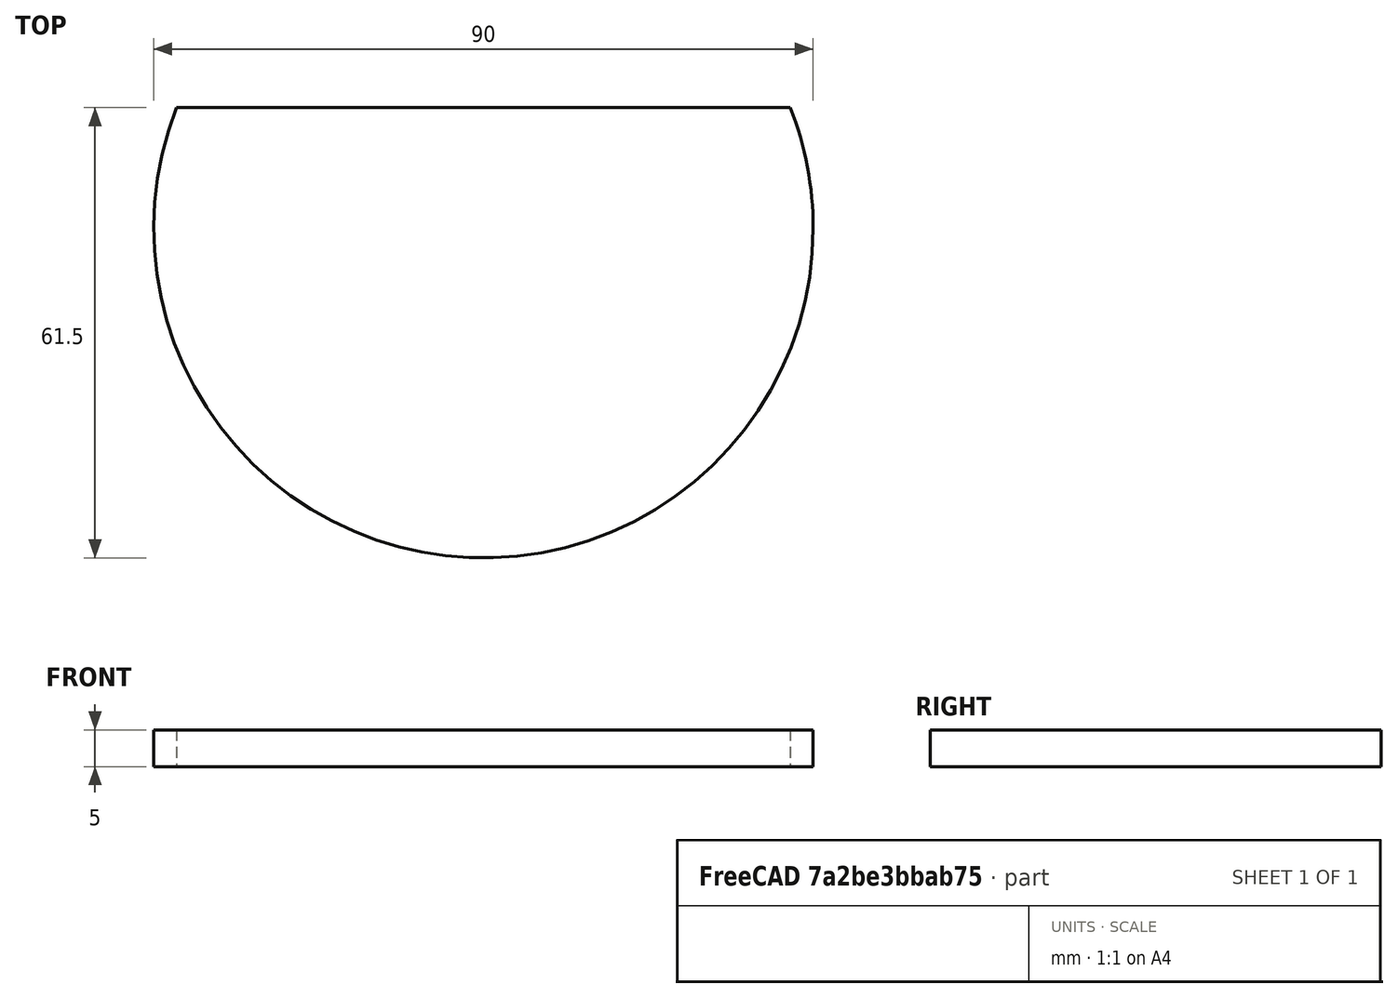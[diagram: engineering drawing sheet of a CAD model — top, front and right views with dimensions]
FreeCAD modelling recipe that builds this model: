
FCSTD DOCUMENT  (FreeCAD 1.0R39319 (Git))
Label: chapa_circle_90mm
License: All rights reserved
LicenseURL: https://en.wikipedia.org/wiki/All_rights_reserved
objects: Sketcher::SketchObject×2, PartDesign::Pad×1, PartDesign::Pocket×1, PartDesign::Body×1
note: 11 computed .brp shape members not serialized (recipe doc carries the construction recipe); baked Part::Feature solids carry a one-line shape summary decoded from their .brp

FEATURE [Sketcher::SketchObject] Sketch_1
  ArcFitTolerance = 1e-06
  AttachmentSupport = -> [XY_Plane]
  FullyConstrained = false
  MakeInternals = false
  MapMode = 5
  sketch-geometry (1):
    g0: Circle CenterX=0 CenterY=0 CenterZ=0 NormalX=0 NormalY=0 NormalZ=1 AngleXU=0 Radius=45
FEATURE [PartDesign::Pad] Pad_1
  Direction = (0,0,1)
  Length = 5
  Length2 = 10
  Profile = -> Sketch_1
  Refine = true
  Suppressed = false
  Type = 0
FEATURE [Sketcher::SketchObject] Sketch_2
  ArcFitTolerance = 1e-06
  AttachmentSupport = -> [Pad_1]
  FullyConstrained = false
  MakeInternals = false
  MapMode = 5
  Placement = pos=(0,0,5) rot=(0,0,1;0rad)
  sketch-geometry (4):
    g0: LineSegment StartX=-67.5 StartY=16.5 StartZ=0 EndX=67.5 EndY=16.5 EndZ=0
    g1: LineSegment StartX=67.5 StartY=16.5 StartZ=0 EndX=67.5 EndY=61.5 EndZ=0
    g2: LineSegment StartX=67.5 StartY=61.5 StartZ=0 EndX=-67.5 EndY=61.5 EndZ=0
    g3: LineSegment StartX=-67.5 StartY=61.5 StartZ=0 EndX=-67.5 EndY=16.5 EndZ=0
  constraints (4):
    c: Coincident(g0,g1)
    c: Coincident(g1,g2)
    c: Coincident(g2,g3)
    c: Coincident(g3,g0)
FEATURE [PartDesign::Pocket] Pocket_2
  BaseFeature = -> Pad_1
  Direction = (0,0,-1)
  Length = 5
  Length2 = 5
  Profile = -> Sketch_2
  Refine = true
  Suppressed = false
  Type = 1
FEATURE [PartDesign::Body] Body
  AllowCompound = false
  Group = -> [Sketch_1,Pad_1,Sketch_2,Pocket_2]
  Origin = -> Origin
  Tip = -> Pocket_2
